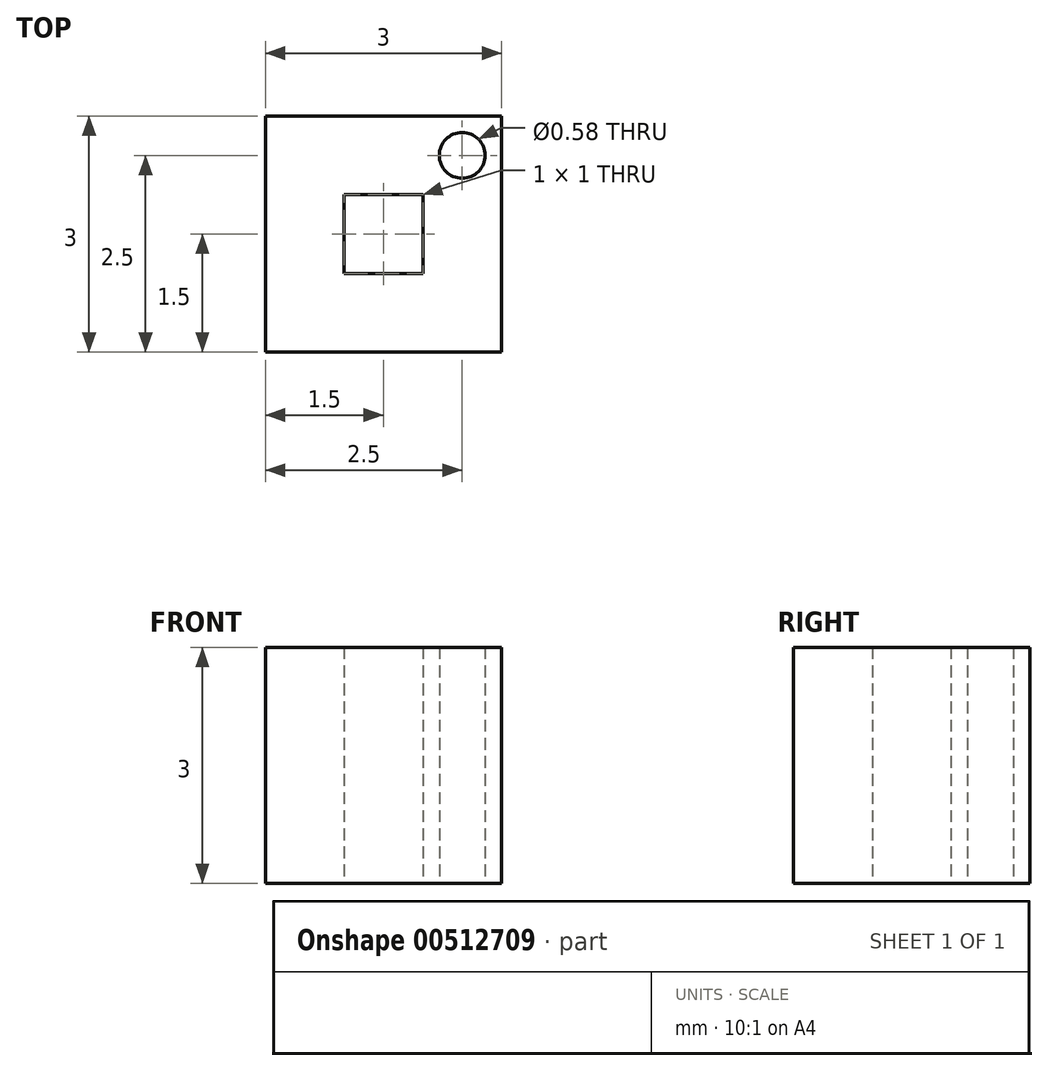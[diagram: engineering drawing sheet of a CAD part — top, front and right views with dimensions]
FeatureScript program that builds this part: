
annotation { "Feature Type Name" : "Feature", "Feature Type Description" : "" }
export const myFeature = defineFeature(function(context is Context, id is Id, definition is map)
    precondition{}
    {
        {
            var Q0;
            Q0=qCreatedBy(makeId("Top.planeOp"),FACE);
            var sketch = newSketch(context, id + "F0", { "sketchPlane" : qUnion([Q0])});
            skLineSegment(sketch, "E0.bottom", {"start": v(0, 0) * mm, "end": v(3, 0) * mm});
            skLineSegment(sketch, "E0.top", {"start": v(0, 3) * mm, "end": v(3, 3) * mm});
            skLineSegment(sketch, "E0.left", {"start": v(0, 0) * mm, "end": v(0, 3) * mm});
            skLineSegment(sketch, "E0.right", {"start": v(3, 0) * mm, "end": v(3, 3) * mm});
            skLineSegment(sketch, "E1.bottom", {"start": v(1, 1) * mm, "end": v(2, 1) * mm});
            skLineSegment(sketch, "E1.top", {"start": v(1, 2) * mm, "end": v(2, 2) * mm});
            skLineSegment(sketch, "E1.left", {"start": v(1, 1) * mm, "end": v(1, 2) * mm});
            skLineSegment(sketch, "E1.right", {"start": v(2, 1) * mm, "end": v(2, 2) * mm});
            skLineSegment(sketch, "E2", {"start": v(2, 2) * mm, "end": v(3, 3) * mm});
            skCircle(sketch, "E3", {"center": v(2.5, 2.5) * mm, "radius": 0.3 * mm});
            skSolve(sketch);
        }
        {
            var Q0;
            Q0=makeQuery(id+"F0.imprint","IMPRINT",FACE,{"disambiguationData":[TD([[makeQuery(id+"F0.imprint","IMPRINT",EDGE,{"derivedFrom":sQuery(id+"F0.wireOp",EDGE,"E0.bottom")}),1.0]])]});
            extrude(context, id + "F1", {"entities" : qUnion([Q0]), "depth" : 3 * mm});
        }
    });
